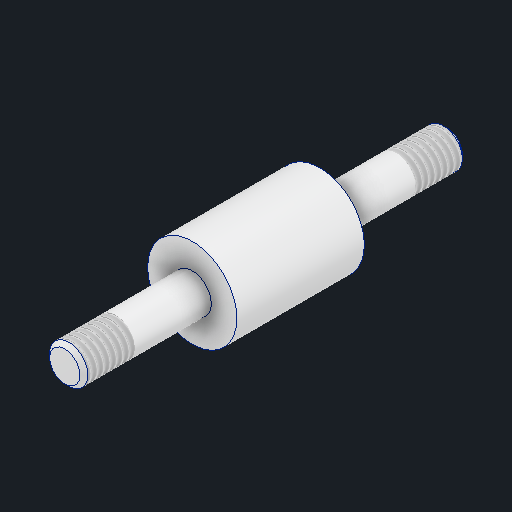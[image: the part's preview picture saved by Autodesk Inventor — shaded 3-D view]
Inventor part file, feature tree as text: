
AUTODESK INVENTOR PART (.ipt)
format: ipt  version: 2025.3 (Build 293356030, 356C)  size: 271,360 bytes
history: native  units: mm
features: thread x2, other x1, revolve x1, chamfer x1, sketch x1
ambient origin geometry x8: Origin, YZ Plane, XZ Plane, XY Plane, X Axis, Y Axis, Z Axis, Center Point
bodies: Body1 (feature_tree)
feature tree (6):
  other  "Sólido1"
  revolve  "Revolución1"  [1 undecoded]
  thread  "Rosca2"  [1 undecoded]
  thread  "Rosca3"  [1 undecoded]
  chamfer  "Chaflán1"  Distance=4.0mm
  sketch  "Boceto1"  dims[d0=7.0mm d1=3.0mm d3=30.0mm d4=90.0deg d7=4.0mm d8=0.0mm d9=4.0mm d10=6.0mm d11=0.306725mm d12=2.0mm d13=45.0deg]
note: 3 required parameter values undecoded (feature->parameter linkage not recoverable at this tier; creation-order binding heuristic only, values carry confidence <= 0.55)